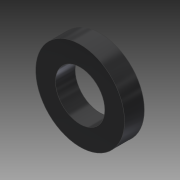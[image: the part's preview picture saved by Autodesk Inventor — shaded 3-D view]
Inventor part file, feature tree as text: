
AUTODESK INVENTOR PART (.ipt)
format: ipt  version: 2014 SP1 (Build 180222100, 222)  size: 78,848 bytes
history: native  units: in
note: dims shown in document units (in); Inventor stores cm internally (conversion verified against a paired STEP export)
features: extrude x1, sketch x1
ambient origin geometry x8: Origin, YZ Plane, XZ Plane, XY Plane, X Axis, Y Axis, Z Axis, Center Point
bodies: Solid1 (feature_tree)
feature tree (2):
  extrude  "Extrusion1"  Depth=0.1in
  sketch  "Sketch1"  dims[d0=0.45in d1=0.25in d2=0.1in d3=0.0in]
